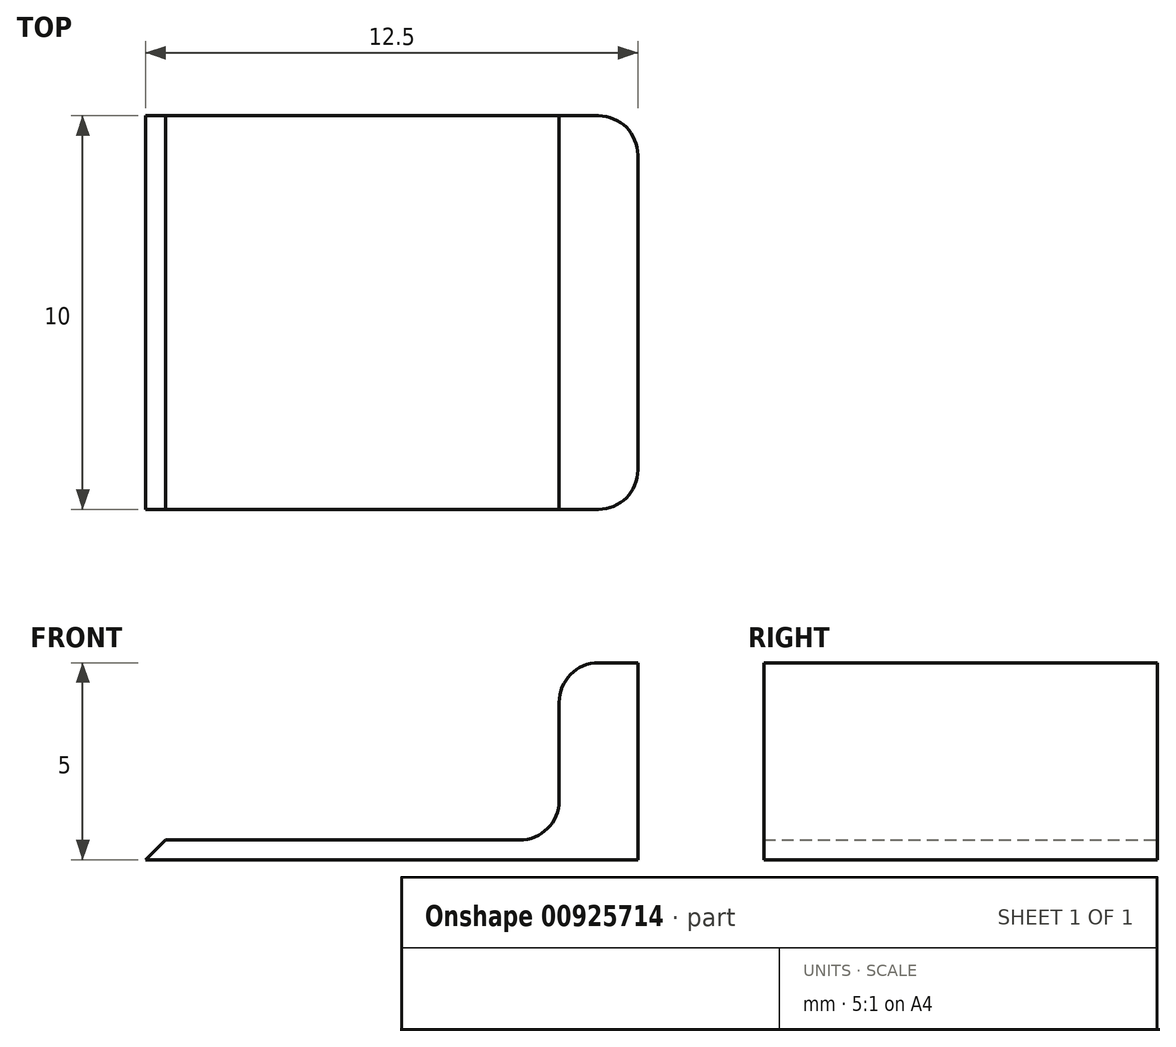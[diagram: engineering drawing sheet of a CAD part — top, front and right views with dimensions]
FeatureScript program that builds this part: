
annotation { "Feature Type Name" : "Feature", "Feature Type Description" : "" }
export const myFeature = defineFeature(function(context is Context, id is Id, definition is map)
    precondition{}
    {
        {
            var Q0;
            Q0=qCreatedBy(makeId("Front.planeOp"),FACE);
            var sketch = newSketch(context, id + "F0", { "sketchPlane" : qUnion([Q0])});
            skLineSegment(sketch, "E0", {"start": v(0, 0) * mm, "end": v(12.5, 0) * mm});
            skLineSegment(sketch, "E1", {"start": v(12.5, 0) * mm, "end": v(12.5, 5) * mm});
            skLineSegment(sketch, "E2", {"start": v(12.5, 5) * mm, "end": v(10.5, 5) * mm});
            skLineSegment(sketch, "E3", {"start": v(10.5, 5) * mm, "end": v(10.5, 0.5) * mm});
            skLineSegment(sketch, "E4", {"start": v(10.5, 0.5) * mm, "end": v(0.5, 0.5) * mm});
            skLineSegment(sketch, "E5", {"start": v(0.5, 0.5) * mm, "end": v(0, 0) * mm});
            skSolve(sketch);
        }
        {
            var Q0;
            Q0 = qSketchRegion(id + "F0", true);
            extrude(context, id + "F1", {"entities" : qUnion([Q0]), "depth" : 10 * mm, "offsetDistance" : 25 * mm});
        }
        {
            var Q0;
            Q0=makeQuery(id+"F1.opExtrude","SWEPT_EDGE",EDGE,{"disambiguationData":[OSD([sQuery(id+"F0.wireOp",EDGE,"E3"),sQuery(id+"F0.wireOp",EDGE,"E4")])]});
            var Q1;
            Q1=makeQuery(id+"F1.opExtrude","CAP_EDGE",EDGE,{"disambiguationData":[OSD([sQuery(id+"F0.wireOp",EDGE,"E1")])],"isStart":false});
            var Q2;
            Q2=makeQuery(id+"F1.opExtrude","CAP_EDGE",EDGE,{"disambiguationData":[OSD([sQuery(id+"F0.wireOp",EDGE,"E1")])],"isStart":true});
            var Q3;
            Q3=makeQuery(id+"F1.opExtrude","SWEPT_EDGE",EDGE,{"disambiguationData":[OSD([sQuery(id+"F0.wireOp",EDGE,"E2"),sQuery(id+"F0.wireOp",EDGE,"E3")])]});
            fillet(context, id + "F2", {"entities" : qUnion([Q0, Q1, Q2, Q3]), "tangentPropagation" : true, "radius" : 1 * mm, "defaultsChanged" : false, "vertexSettings" : [], "allowEdgeOverflow" : false});
        }
    });
